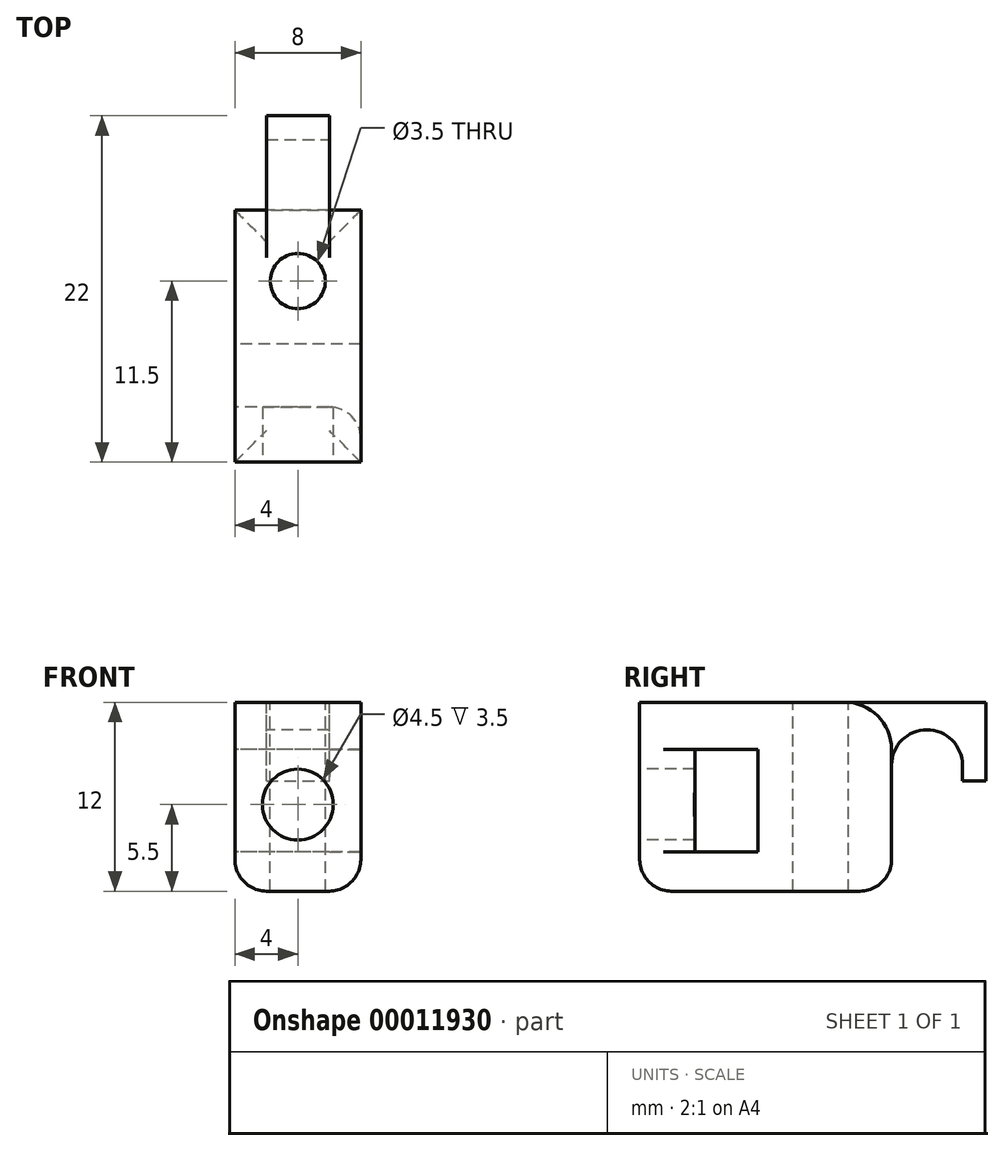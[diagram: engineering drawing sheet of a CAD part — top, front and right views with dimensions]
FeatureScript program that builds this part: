
annotation { "Feature Type Name" : "Feature", "Feature Type Description" : "" }
export const myFeature = defineFeature(function(context is Context, id is Id, definition is map)
    precondition{}
    {
        {
            var Q0;
            Q0=qCreatedBy(makeId("Top.planeOp"),FACE);
            var sketch = newSketch(context, id + "F0", { "sketchPlane" : qUnion([Q0])});
            skLineSegment(sketch, "E0.rect.bottom", {"start": v(-4, 8) * mm, "end": v(4, 8) * mm});
            skLineSegment(sketch, "E0.rect.top", {"start": v(-4, -8) * mm, "end": v(4, -8) * mm});
            skLineSegment(sketch, "E0.rect.left", {"start": v(-4, 8) * mm, "end": v(-4, -8) * mm});
            skLineSegment(sketch, "E0.rect.right", {"start": v(4, 8) * mm, "end": v(4, -8) * mm});
            skPoint(sketch, "E0.rect.middle", {"position": v(0, 0) * mm});
            skSolve(sketch);
        }
        {
            var Q0;
            Q0=makeQuery(id+"F0.imprint","IMPRINT",FACE,{"disambiguationData":[TD([[makeQuery(id+"F0.imprint","IMPRINT",EDGE,{"derivedFrom":sQuery(id+"F0.wireOp",EDGE,"E0.rect.bottom")}),-1.0]])]});
            extrude(context, id + "F1", {"entities" : qUnion([Q0]), "depth" : 12 * mm});
        }
        {
            var Q0;
            Q0=makeQuery(id+"F1.opExtrude","CAP_FACE",FACE,{"disambiguationData":[OSD([sQuery(id+"F0.wireOp",EDGE,"E0.rect.bottom"),sQuery(id+"F0.wireOp",EDGE,"E0.rect.top"),sQuery(id+"F0.wireOp",EDGE,"E0.rect.left"),sQuery(id+"F0.wireOp",EDGE,"E0.rect.right")])],"isStart":false});
            var sketch = newSketch(context, id + "F2", { "sketchPlane" : qUnion([Q0])});
            skCircle(sketch, "E1", {"center": v(0, 3.5) * mm, "radius": 1.75 * mm});
            skSolve(sketch);
        }
        {
            var Q0;
            Q0=makeQuery(id+"F1.opExtrude","SWEPT_FACE",FACE,{"disambiguationData":[OSD([sQuery(id+"F0.wireOp",EDGE,"E0.rect.left")])]});
            var sketch = newSketch(context, id + "F3", { "sketchPlane" : qUnion([Q0])});
            skLineSegment(sketch, "E2.bottom", {"start": v(0.5, 9) * mm, "end": v(4.5, 9) * mm});
            skLineSegment(sketch, "E2.top", {"start": v(0.5, 2.5) * mm, "end": v(4.5, 2.5) * mm});
            skLineSegment(sketch, "E2.left", {"start": v(0.5, 9) * mm, "end": v(0.5, 2.5) * mm});
            skLineSegment(sketch, "E2.right", {"start": v(4.5, 9) * mm, "end": v(4.5, 2.5) * mm});
            skSolve(sketch);
        }
        {
            var Q0;
            Q0=qSketchRegion(id+"F3",true);
            extrude(context, id + "F4", {"entities" : qUnion([Q0]), "operationType" : NewBodyOperationType.REMOVE, "endBound" : BoundingType.THROUGH_ALL, "oppositeDirection" : true, "depth" : 25 * mm});
        }
        {
            var Q0;
            Q0=makeQuery(id+"F4.boolean.opBoolean","COPY",EDGE,{"derivedFrom":makeQuery(id+"F4.opExtrude","CAP_EDGE",EDGE,{"disambiguationData":[OSD([sQuery(id+"F3.wireOp",EDGE,"E2.right")])],"isStart":true})});
            var Q1;
            Q1=makeQuery(id+"F4.boolean.opBoolean","INTERSECT",EDGE,{"derivedFrom":[makeQuery(id+"F1.opExtrude","SWEPT_FACE",FACE,{"disambiguationData":[OSD([sQuery(id+"F0.wireOp",EDGE,"E0.rect.right")])]}),makeQuery(id+"F4.opExtrude","SWEPT_FACE",FACE,{"disambiguationData":[OSD([sQuery(id+"F3.wireOp",EDGE,"E2.right")])]})]});
            var Q2;
            Q2=makeQuery(id+"F1.opExtrude","CAP_EDGE",EDGE,{"disambiguationData":[OSD([sQuery(id+"F0.wireOp",EDGE,"E0.rect.top")])],"isStart":true});
            var Q3;
            Q3=makeQuery(id+"F1.opExtrude","CAP_EDGE",EDGE,{"disambiguationData":[OSD([sQuery(id+"F0.wireOp",EDGE,"E0.rect.bottom")])],"isStart":true});
            var Q4;
            Q4=makeQuery(id+"F1.opExtrude","CAP_EDGE",EDGE,{"disambiguationData":[OSD([sQuery(id+"F0.wireOp",EDGE,"E0.rect.right")])],"isStart":true});
            var Q5;
            Q5=makeQuery(id+"F1.opExtrude","CAP_EDGE",EDGE,{"disambiguationData":[OSD([sQuery(id+"F0.wireOp",EDGE,"E0.rect.left")])],"isStart":true});
            fillet(context, id + "F5", {"entities" : qUnion([Q0, Q1, Q2, Q3, Q4, Q5]), "radius" : 2 * mm, "tangentPropagation" : true, "allowEdgeOverflow" : false});
        }
        {
            var Q0;
            Q0=makeQuery(id+"F2.imprint","IMPRINT",FACE,{"disambiguationData":[TD([[makeQuery(id+"F2.imprint","IMPRINT",EDGE,{"derivedFrom":sQuery(id+"F2.wireOp",EDGE,"E1")}),1.0]])]});
            extrude(context, id + "F6", {"entities" : qUnion([Q0]), "operationType" : NewBodyOperationType.REMOVE, "endBound" : BoundingType.THROUGH_ALL, "oppositeDirection" : true, "depth" : 25 * mm});
        }
        {
            var Q0;
            Q0=makeQuery(id+"F1.opExtrude","SWEPT_FACE",FACE,{"disambiguationData":[OSD([sQuery(id+"F0.wireOp",EDGE,"E0.rect.top")])]});
            var sketch = newSketch(context, id + "F7", { "sketchPlane" : qUnion([Q0])});
            skCircle(sketch, "E3", {"center": v(0, 5.5) * mm, "radius": 2.25 * mm});
            skSolve(sketch);
        }
        {
            var Q0;
            Q0 = qSketchRegion(id + "F7", true);
            extrude(context, id + "F8", {"entities" : qUnion([Q0]), "operationType" : NewBodyOperationType.REMOVE, "oppositeDirection" : true, "depth" : 4 * mm});
        }
        {
            var Q0;
            Q0=makeQuery(id+"F1.opExtrude","CAP_FACE",FACE,{"disambiguationData":[OSD([sQuery(id+"F0.wireOp",EDGE,"E0.rect.bottom"),sQuery(id+"F0.wireOp",EDGE,"E0.rect.top"),sQuery(id+"F0.wireOp",EDGE,"E0.rect.left"),sQuery(id+"F0.wireOp",EDGE,"E0.rect.right")])],"isStart":false});
            var sketch = newSketch(context, id + "F9", { "sketchPlane" : qUnion([Q0])});
            skLineSegment(sketch, "E4.bottom", {"start": v(-2, 8) * mm, "end": v(2, 8) * mm});
            skLineSegment(sketch, "E4.top", {"start": v(-2, 14) * mm, "end": v(2, 14) * mm});
            skLineSegment(sketch, "E4.left", {"start": v(-2, 8) * mm, "end": v(-2, 14) * mm});
            skLineSegment(sketch, "E4.right", {"start": v(2, 8) * mm, "end": v(2, 14) * mm});
            skPoint(sketch, "E5", {"position": v(0, 14) * mm});
            skSolve(sketch);
        }
        {
            var Q0;
            Q0 = qSketchRegion(id + "F9", true);
            extrude(context, id + "F10", {"entities" : qUnion([Q0]), "operationType" : NewBodyOperationType.ADD, "oppositeDirection" : true, "depth" : 5 * mm});
        }
        {
            var Q0;
            Q0=makeQuery(id+"F10.opExtrude","SWEPT_FACE",FACE,{"disambiguationData":[OSD([sQuery(id+"F9.wireOp",EDGE,"E4.left")])]});
            var sketch = newSketch(context, id + "F11", { "sketchPlane" : qUnion([Q0])});
            skLineSegment(sketch, "E6", {"start": v(-8, 7) * mm, "end": v(-8, 8) * mm});
            skArc(sketch, "E7", {"start": v(-8, 8) * mm, "mid": v(-10.25, 10.25) * mm, "end": v(-12.5, 8) * mm});
            skLineSegment(sketch, "E8", {"start": v(-12.5, 8) * mm, "end": v(-12.5, 7) * mm});
            skLineSegment(sketch, "E9", {"start": v(-8, 7) * mm, "end": v(-8, 6.04) * mm});
            skLineSegment(sketch, "E10", {"start": v(-8, 6.04) * mm, "end": v(-12.5, 6.04) * mm});
            skLineSegment(sketch, "E11", {"start": v(-12.5, 6.04) * mm, "end": v(-12.5, 7) * mm});
            skSolve(sketch);
        }
        {
            var Q0;
            Q0 = qSketchRegion(id + "F11", true);
            extrude(context, id + "F12", {"entities" : qUnion([Q0]), "operationType" : NewBodyOperationType.REMOVE, "oppositeDirection" : true, "depth" : 25 * mm});
        }
        {
            var Q0;
            {var subQ0=sQuery(id+"F0.wireOp",EDGE,"E0.rect.bottom");var subQ2=sQuery(id+"F0.wireOp",EDGE,"E0.rect.left");Q0=makeQuery(id+"F10.boolean.opBoolean","SPLIT",EDGE,{"disambiguationData":[TD([makeQuery(id+"F1.opExtrude","SWEPT_FACE",FACE,{"disambiguationData":[OSD([subQ2])]})])],"derivedFrom":makeQuery(id+"F1.opExtrude","CAP_EDGE",EDGE,{"disambiguationData":[OSD([subQ0])],"isStart":false})});}
            var Q1;
            {var subQ0=sQuery(id+"F0.wireOp",EDGE,"E0.rect.bottom");var subQ2=sQuery(id+"F0.wireOp",EDGE,"E0.rect.right");Q1=makeQuery(id+"F10.boolean.opBoolean","SPLIT",EDGE,{"disambiguationData":[TD([makeQuery(id+"F1.opExtrude","SWEPT_FACE",FACE,{"disambiguationData":[OSD([subQ2])]})])],"derivedFrom":makeQuery(id+"F1.opExtrude","CAP_EDGE",EDGE,{"disambiguationData":[OSD([subQ0])],"isStart":false})});}
            fillet(context, id + "F13", {"entities" : qUnion([Q0, Q1]), "radius" : 3 * mm, "tangentPropagation" : true, "allowEdgeOverflow" : false});
        }
    });
